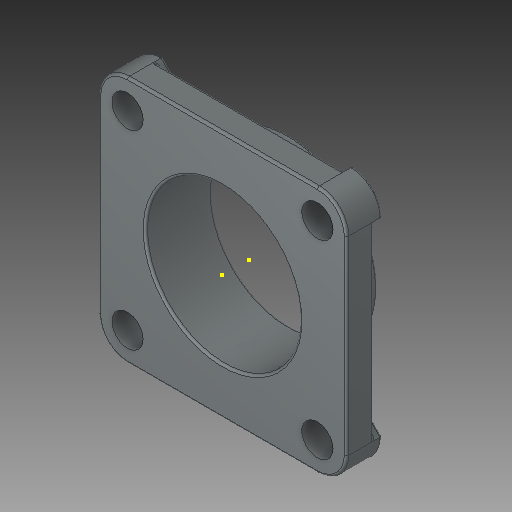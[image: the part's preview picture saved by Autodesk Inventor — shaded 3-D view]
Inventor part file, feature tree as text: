
AUTODESK INVENTOR PART (.ipt)
format: ipt  version: 2019 (Build 230136000, 136)  size: 448,000 bytes
history: native  units: in
note: dims shown in document units (in); Inventor stores cm internally (conversion verified against a paired STEP export)
features: sketch x10, other x3
ambient origin geometry x8: Origin, YZ Plane, XZ Plane, XY Plane, X Axis, Y Axis, Z Axis, Center Point
bodies: Solid1 (feature_tree)
feature tree (13):
  other  "project flange bearing part1.ipt"
  other  "Solid1::project flange bearing part1.ipt"
  other  "TaggingFeature1"
  sketch  "Sketch1"  dims[d0=0.3937in]
  sketch  "Sketch2"
  sketch  "Sketch3"
  sketch  "Sketch4"
  sketch  "Sketch5"
  sketch  "Sketch6"
  sketch  "Sketch7"
  sketch  "Sketch8"
  sketch  "Sketch9"
  sketch  "Sketch10"
